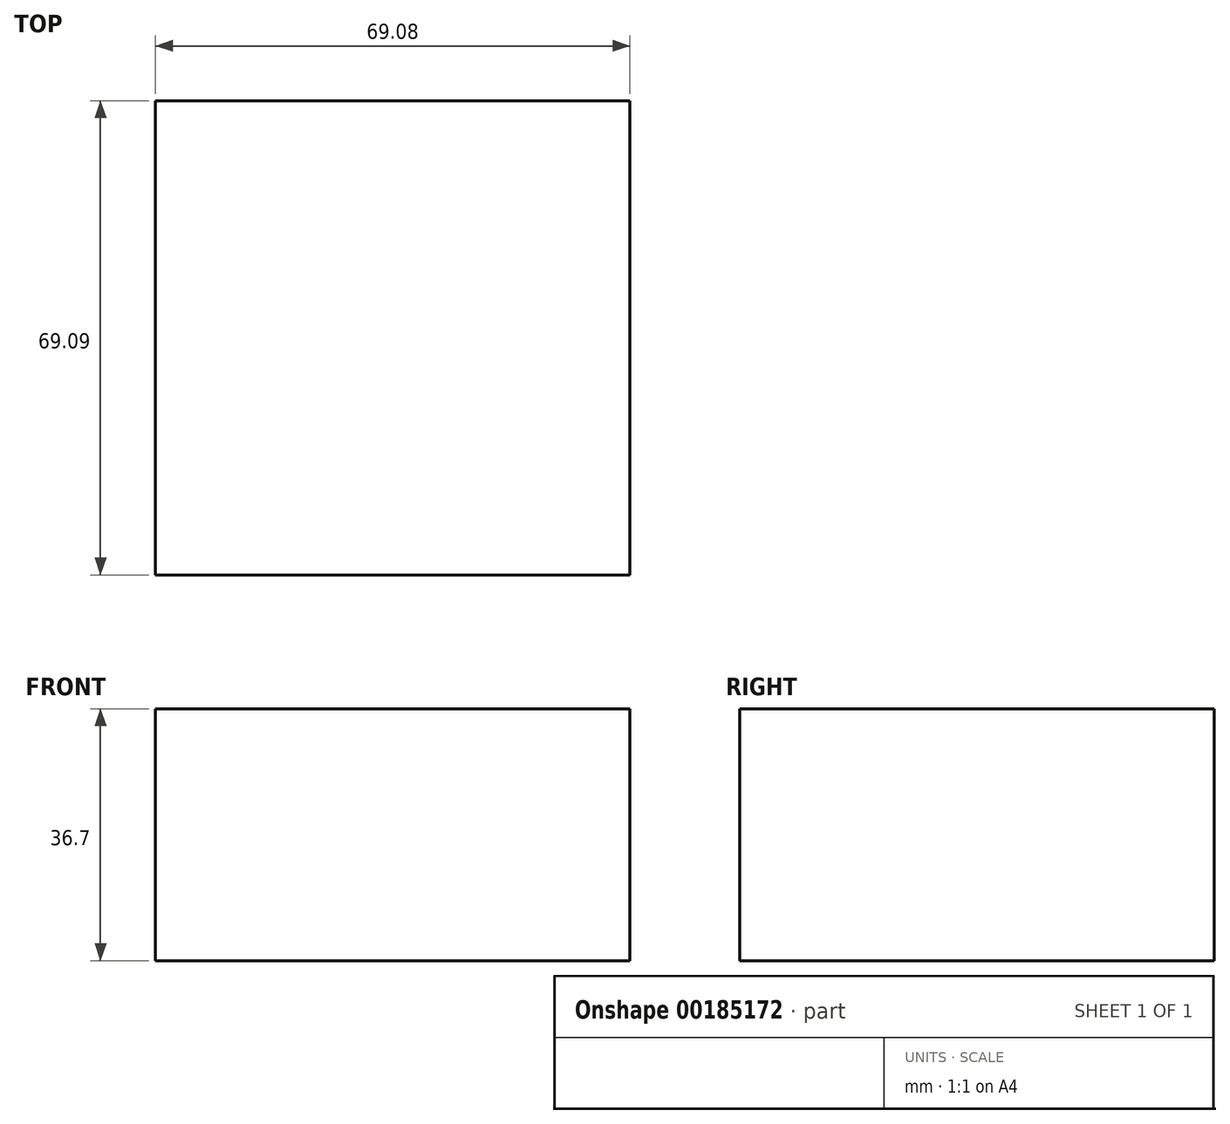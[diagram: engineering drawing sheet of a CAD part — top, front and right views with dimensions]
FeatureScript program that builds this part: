
annotation { "Feature Type Name" : "Feature", "Feature Type Description" : "" }
export const myFeature = defineFeature(function(context is Context, id is Id, definition is map)
    precondition{}
    {
        {
            var Q0;
            Q0=qCreatedBy(makeId("Top.planeOp"),FACE);
            var sketch = newSketch(context, id + "F0", { "sketchPlane" : qUnion([Q0])});
            skLineSegment(sketch, "E0.bottom", {"start": v(-27.88, 29.95) * mm, "end": v(41.2, 29.95) * mm});
            skLineSegment(sketch, "E0.top", {"start": v(-27.88, -39.14) * mm, "end": v(41.2, -39.14) * mm});
            skLineSegment(sketch, "E0.left", {"start": v(-27.88, 29.95) * mm, "end": v(-27.88, -39.14) * mm});
            skLineSegment(sketch, "E0.right", {"start": v(41.2, 29.95) * mm, "end": v(41.2, -39.14) * mm});
            skSolve(sketch);
        }
        {
            var Q0;
            Q0=makeQuery(id+"F0.imprint","IMPRINT",FACE,{"disambiguationData":[TD([[makeQuery(id+"F0.imprint","IMPRINT",EDGE,{"derivedFrom":sQuery(id+"F0.wireOp",EDGE,"E0.bottom")}),-1.0]])]});
            extrude(context, id + "F1", {"entities" : qUnion([Q0]), "depth" : 36.7 * mm});
        }
    });
